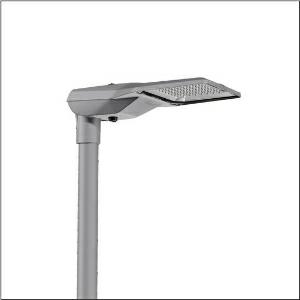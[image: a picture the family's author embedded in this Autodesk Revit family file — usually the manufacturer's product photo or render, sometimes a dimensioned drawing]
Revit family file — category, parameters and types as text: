
# Revit family: streetlight_sl_21_iq_midi___st1_5a_5xe3p31y08mb_5967
name_source: partatom
category: Lighting Fixtures
units: mm (PartAtom-declared; Revit-internal decimal feet)

## family parameters
Cut with Voids When Loaded = No
Host = Face
Light Source = No
Part Type = Normal
Room Calculation Point = No
Round Connector Dimension = Use Diameter
Shared = No

## types (1)
- --- (1 x LED, 18020 lm, 129.3 W, 3000K)
    Apparent Load = 129 VA
    CIE Flux Codes = 22 53 95 100 100
    Color Rendering = 70
    Color Temperature = 3000K
    Default Elevation = 1800 mm
    Description = Streetlight SL 21 iQ midi, mast luminaire, primary light control with lens, of PMMA, primary optical cover: cover, of toughened safety glass, transparent, light distribution: ST1.5a, light emission: direct distribution, primary light characteristic: asymmetric, installation type: post-top, side-entry, LED, High Power LED, rated luminous flux: 18.020lm, luminous efficacy: 139lm/W, light colour: 730, colour temperature: 3000K, control gear: iQ-Street Remote, D4i with power reduction, control: pre-setting: logarithmic dimming characteristic, Street-Remote, Auto-Match, Temp-Guard, Lumen-Switch, Night-Set, Smart-Wire, Light-Fading, Desk-Remote (wireless, voltage-free reading and setting of iQ features in the workshop via application-optimized NFC function/RFID function), optimised constant luminous flux control (CLO 2.0), mains connection: 230..240V, AC, 50/60Hz, start of lifetime: 129W, end of service life: 142W, reduction: 56W, luminaire housing, of diecast aluminium, powder-coated, SITECO metallic grey (DB 702S), corrosivity category C5 high according to DIN EN ISO 12944, please order mast flange separately, inclination adjustable: 0°, 5°, 10°, 15°, sealing non-destructively replaceable, multi-level sealing system, length: 644mm, width: 335mm, height: 110mm, mast flange for spigot size: 42mm (side-entry): 5XC10008XM4, 60/48mm (side-entry/post-top): 5XC10108XM2, 76/60mm (side-entry/post-top): 5XC10108XM1, mounting height: 4..8m, Smart Interface below and above, protection rating (complete): IP66, insulation class (complete): insulation class II (safety insulation), certification: CE, ENEC, ENEC+, VDE, impact resistance: IK10, permissible operating ambient temperature for outdoor applications: -40..+50°C, standard-compliant lighting for roads and squares, packaging unit: 1 piece

Light Distribution: ST1.5a
    Height = 111 mm
    Lamp = 1 x LED
    Lamp Light Flux = 18020 lm
    Lamp Power = 129.3 W
    Lamp count = 1
    Length = 644 mm
    Luminous efficacy = 139 lm/W
    Manufacturer = Siteco
    ModVariant = No
    Model = 5XE3P31Y08MB
    Number of Poles = 1
    OnlyDefault = Yes
    Power Factor = 1
    Product Name = Streetlight SL 21 iQ midi | ST1.5a
    Product group = mast luminaire | pylon top
    ProductGroupID = 6100
    Protection Class = Protection class II
    Protection Degree = IP 66
    RLX_Detail_Level = 1
    RLX_Emergency_Light_Flux = 0 lm
    RLX_Emergency_Type = 0
    RLX_Emergency_Type_DB = No
    RlxData = <blob elided: 95353 chars, md5=85726138>
    Socket = socket
    Standby Power = 0 W
    System Light Flux = 18021 lm
    System Power = 129 W
    Type Comments = factory setting: luminous flux: 100 % | dim-lin: 254 | 672 mA
    Type Image = l_1004304.jpg
    URL = http://relux.com
    VarID = @adj_111813
    Voltage = 0 V
    Weight = 0.00 kg
    Width = 336 mm

## geometry (parser evidence)
native form markers: Blend x4, Sweep x9
no freeform markers — native parametric forms only
